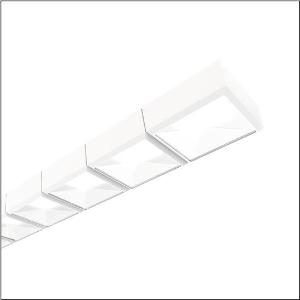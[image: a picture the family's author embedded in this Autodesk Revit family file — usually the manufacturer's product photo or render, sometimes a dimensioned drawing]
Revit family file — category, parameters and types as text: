
# Revit family: scriptus_r__11_5mz223d04wa_758a
name_source: partatom
category: Lighting Fixtures
units: mm (PartAtom-declared; Revit-internal decimal feet)

## family parameters
Cut with Voids When Loaded = No
Host = Face
Light Source = No
Part Type = Normal
Room Calculation Point = No
Round Connector Dimension = Use Diameter
Shared = No

## types (1)
- --- (1 x LED 4000K / CRI = 80 (unbekannt), 7230 lm, 4000K)
    Apparent Load = 51 VA
    CIE Flux Codes = 82 95 99 100 100
    Color Rendering = 80
    Color Temperature = 4000K
    Default Elevation = 1800 mm
    Description = Scriptus® 11, office luminaire, primary optical cover: lenses, CAT 2 (L<= 3000cd/m²), light emission: direct distribution, primary light characteristic: symmetric, installation type: surface-mounted, LED, rated luminous flux: 7.230lm, luminous efficacy: 143lm/W, light colour: 840, colour temperature: 4000K, control gear: ECG DALI, with terminal, 5-pole, mains connection: 230V, AC, 50Hz, rated input power: 51W, housing, luminaire housing, of aluminium, traffic white (RAL 9016), length: 2.426mm, width: 114mm, height: 57mm, protection rating (complete): IP20, insulation class (complete): insulation class I (protective earthing), certification: CE, ENEC, VDE, protection symbol: F, permissible operating ambient temperature: 0..+35°C, standard: EN 50419, packaging unit: 1 piece
    Height = 57 mm
    Lamp = 1 x LED 4000K / CRI >= 80 (unbekannt)
    Lamp Light Flux = 7230 lm
    Lamp count = 1
    Length = 2426 mm
    Luminous efficacy = 143 lm/W
    Manufacturer = Siteco
    ModVariant = No
    Model = 5MZ223D04WA
    Mounting Place = Ceiling
    Mounting Type = Surface mounted
    Number of Poles = 1
    OnlyDefault = Yes
    Power Factor = 1
    Product Name = Scriptus® 11
    Product group = office luminaire | ceiling mounted
    ProductGroupID = 304
    Protection Class = Protection class I
    Protection Degree = IP 20
    RLX_Detail_Level = 1
    RLX_Emergency_Light_Flux = 0 lm
    RLX_Emergency_Type = 0
    RLX_Emergency_Type_DB = No
    RlxData = <blob elided: 31325 chars, md5=50c8d24a>
    Socket = socket
    Standby Power = 0 W
    System Light Flux = 7230 lm
    System Power = 51 W
    Type Comments = factory setting: luminous flux: 100 % | dim-lin: 254 | 525 mA
    Type Image = l_1004833.jpg
    URL = http://relux.com
    VarID = @adj_149105
    Voltage = 0 V
    Weight = 0.00 kg
    Width = 114 mm

## geometry (parser evidence)
native form markers: Blend x4, Sweep x11
no freeform markers — native parametric forms only
